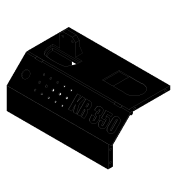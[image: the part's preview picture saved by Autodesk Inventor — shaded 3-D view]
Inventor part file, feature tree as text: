
AUTODESK INVENTOR PART (.ipt)
format: ipt  version: 2020 (Build 240168000, 168)  size: 1,130,496 bytes
history: native  units: mm
features: sketch x33, extrude x30, projected_geometry x20, chamfer x5, plane x3, emboss x1
ambient origin geometry x8: Origin, YZ Plane, XZ Plane, XY Plane, X Axis, Y Axis, Z Axis, Center Point
bodies: Solid1 (feature_tree)
feature tree (92):
  extrude  "Extrusion1"  Depth=120.0mm
  extrude  "Extrusion2"  Depth=40.0mm
  extrude  "Extrusion3"  TaperAngle=135.0deg  [1 undecoded]
  extrude  "Extrusion4"  Depth=125.0mm
  extrude  "Extrusion5"  Depth=1.0mm
  extrude  "Extrusion6"  Depth=20.0mm
  extrude  "Extrusion7"  Depth=10.0mm TaperAngle=0.0deg
  extrude  "Extrusion8"  Depth=3.0mm
  extrude  "Extrusion9"  Depth=0.25mm
  extrude  "Extrusion10"  Depth=0.25mm
  extrude  "Extrusion11"  Depth=0.3mm
  extrude  "Extrusion17"  Depth=20.0mm TaperAngle=0.0deg
  extrude  "Extrusion18"  Depth=14.196mm
  extrude  "Extrusion19"  Depth=0.35mm TaperAngle=0.0deg
  extrude  "Extrusion20"  Depth=19.547688mm
  extrude  "Extrusion21"  Depth=0.3mm
  extrude  "Extrusion22"  Depth=0.3mm
  extrude  "Extrusion23"  Depth=0.3mm
  extrude  "Extrusion24"  Depth=0.3mm
  sketch  "Sketch25"  dims[d73=0.3mm d74=5.0mm d75=0.25mm d76=19.547688mm d77=0.35mm d78=0.0mm]
  chamfer  "Chamfer1"  Distance=20.0mm
  chamfer  "Chamfer2"  Distance=0.35mm
  sketch  "Sketch26"  dims[d79=0.3mm d80=5.0mm d81=0.25mm d82=19.547688mm d83=20.0mm d84=0.0mm]
  extrude  "Extrusion25"  Depth=20.0mm TaperAngle=0.0deg
  emboss  "Emboss1"
  plane  "Work Plane1"
  extrude  "Extrusion26"  Depth=10.0mm TaperAngle=0.0deg
  plane  "Work Plane2"
  extrude  "Extrusion27"  Depth=10.0mm TaperAngle=0.0deg
  plane  "Work Plane3"
  extrude  "Extrusion28"  Depth=10.0mm
  extrude  "Extrusion29"  Depth=10.0mm
  chamfer  "Chamfer3"  Distance=10.0mm
  extrude  "Extrusion30"  Depth=15.0mm
  extrude  "Extrusion31"  Depth=15.0mm
  extrude  "Extrusion32"  Depth=6.0mm
  extrude  "Extrusion33"  Depth=15.0mm
  extrude  "Extrusion34"  Depth=4.2mm
  chamfer  "Chamfer4"  Distance=3.0mm
  chamfer  "Chamfer5"  Distance=6.0mm
  extrude  "Extrusion35"  Depth=10.0mm
  sketch  "Sketch1"  dims[d0=55.0mm d1=120.0mm]
  sketch  "Sketch2"  dims[d2=50.0mm d3=40.0mm]
  projected_geometry  "Projected Loop1"
  sketch  "Sketch3"  dims[d4=135.0deg d5=135.0deg]
  sketch  "Sketch4"  dims[d6=5.0mm d7=125.0mm]
  projected_geometry  "Projected Loop2"
  projected_geometry  "Projected Loop3"
  sketch  "Sketch5"  dims[d8=190.0mm d9=1.0mm]
  sketch  "Sketch6"  dims[d10=1.0mm d11=20.0mm]
  sketch  "Sketch7"  dims[d12=3.0mm d13=10.0mm d14=0.0mm]
  sketch  "Sketch8"  dims[d15=3.0mm d16=0.3mm]
  sketch  "Sketch9"  dims[d18=5.0mm d19=0.25mm]
  sketch  "Sketch10"  dims[d21=0.25mm d22=0.25mm]
  sketch  "Sketch11"  dims[d23=0.0mm d24=0.0mm d25=0.3mm d26=5.0mm d27=0.25mm]
  sketch  "Sketch17"  dims[d28=2.0mm d29=20.0mm d30=0.0mm]
  projected_geometry  "Projected Loop7"
  sketch  "Sketch18"  dims[d36=5.0mm d37=14.196mm]
  sketch  "Sketch19"  dims[d38=0.3mm d39=5.0mm d40=0.25mm d41=0.35mm d42=0.0mm]
  projected_geometry  "Projected Loop8"
  sketch  "Sketch20"  dims[d43=0.3mm d44=5.0mm d45=0.25mm d46=19.547688mm]
  sketch  "Sketch21"  dims[d47=20.0mm d48=0.0mm d49=0.3mm d50=5.0mm d51=0.25mm d52=19.547688mm]
  projected_geometry  "Projected Loop9"
  projected_geometry  "Projected Loop10"
  sketch  "Sketch22"  dims[d53=0.35mm d54=0.0mm d55=0.3mm d56=5.0mm d57=0.25mm d58=19.547688mm]
  projected_geometry  "Projected Loop11"
  projected_geometry  "Projected Loop12"
  projected_geometry  "Projected Loop13"
  projected_geometry  "Projected Loop14"
  sketch  "Sketch23"  dims[d59=228.6mm d60=0.0mm d61=0.3mm d62=5.0mm d63=0.25mm d64=19.547688mm]
  sketch  "Sketch24"  dims[d65=0.35mm d66=0.0mm d67=0.3mm d68=5.0mm d69=0.25mm d70=19.547688mm d71=20.0mm d72=0.0mm]
  projected_geometry  "Projected Loop15"
  projected_geometry  "Projected Loop16"
  projected_geometry  "Projected Loop17"
  projected_geometry  "Projected Loop18"
  projected_geometry  "Projected Loop19"
  projected_geometry  "Projected Loop20"
  sketch  "Sketch27"  dims[d96=3.0mm d107=10.0mm d108=0.0mm]
  sketch  "Sketch28"  dims[d109=12.0mm d110=10.0mm d111=0.0mm]
  sketch  "Sketch29"  dims[d112=10.0mm d113=0.0mm d114=12.0mm]
  sketch  "Sketch30"  dims[d115=5.5mm d116=3.25mm d117=10.0mm d118=0.0mm]
  projected_geometry  "Projected Loop21"
  sketch  "Sketch31"  dims[d119=6.0mm d120=15.0mm]
  projected_geometry  "Projected Loop22"
  sketch  "Sketch32"  dims[d121=6.0mm d122=15.0mm]
  sketch  "Sketch33"  dims[d123=6.0mm d124=6.0mm]
  sketch  "Sketch34"  dims[d125=15.0mm d126=15.0mm]
  projected_geometry  "Projected Loop23"
  sketch  "Sketch35"  dims[d127=4.0mm d128=0.0mm d129=4.2mm]
  sketch  "Sketch36"  dims[d130=4.2mm]
  sketch  "Sketch37"  dims[d131=4.2mm]
  sketch  "Sketch38"  dims[d132=4.2mm d133=3.0mm d134=0.0mm d135=6.0mm d136=6.0mm d137=15.0mm d138=15.0mm d139=4.0mm d140=0.0mm d141=4.2mm d142=4.2mm d143=3.0mm d144=0.0mm d145=2.0mm d146=4.0mm d147=45.0deg d148=2.0mm d149=4.0mm d150=45.0deg d151=22.2mm d152=6.4mm d153=6.4mm d154=6.4mm d155=6.4mm d156=6.4mm d157=30.0mm d158=40.0mm d159=43.2mm d160=21.4mm d161=21.4mm d162=21.4mm d163=21.4mm d164=10.0mm d165=13.2mm d166=0.0mm d167=0.0mm d168=5.1mm d169=5.1mm d170=5.1mm d171=5.1mm d172=5.1mm d173=3.0mm d174=0.0mm d175=22.2mm d176=6.4mm d177=6.4mm d178=6.4mm d179=6.4mm d180=6.4mm d181=30.0mm d182=40.0mm d183=43.2mm d184=21.4mm d185=21.4mm d186=21.4mm d187=21.4mm d188=10.0mm d189=13.2mm d190=0.0mm d191=0.0mm d192=5.1mm d193=5.1mm d194=5.1mm d195=5.1mm d196=5.1mm d197=1.0mm d198=0.0mm d199=5.2mm d200=50.0mm d201=6.0mm d202=10.0mm d203=3.0mm d204=10.0mm d205=0.0mm d206=160.0mm d207=10.0mm d208=0.0mm d209=266.0mm d210=10.0mm d211=0.0mm d212=6.0mm d213=6.0mm d214=6.0mm d215=10.0mm d216=0.0mm d217=10.0mm d218=4.0mm d219=45.0deg d299=27.0mm d300=67.21989mm d301=67.21989mm d302=52.0mm d303=74.5mm d304=26.0mm d305=26.0mm d306=121.0mm d307=0.25mm d308=0.25mm d309=0.25mm d310=0.25mm d311=3.5mm d312=0.0mm d313=32.75mm d314=2.5mm d315=0.0mm d316=72.0mm d317=91.999999mm d318=81.999999mm d319=167.166667mm d320=45.750001mm d321=45.750001mm d322=50.750001mm d323=172.166667mm d324=50.750001mm d325=7.0mm d326=7.0mm d327=2.0mm d328=2.0mm d329=5.0mm d330=32.384967mm d331=32.384967mm d332=22.0mm d333=0.15mm d334=5.0mm d335=0.0mm d336=72.0mm d337=91.999999mm d338=81.999999mm d339=167.166667mm d340=45.750001mm d341=45.750001mm d342=50.750001mm d343=172.166667mm d344=50.750001mm d345=7.0mm d346=7.0mm d347=2.0mm d348=2.0mm d349=5.0mm d350=32.384967mm d351=32.384967mm d352=22.0mm d353=0.15mm d354=5.0mm d355=0.0mm d356=50.0mm d357=21.15mm d358=50.0mm d359=0.0mm d360=10.0mm d361=25.0mm d362=45.0deg d363=10.0mm d364=25.0mm d365=45.0deg d366=50.0mm d367=12.5mm d368=5.5mm d369=5.5mm d370=15.0mm d371=15.0mm d372=0.0mm d373=0.0mm d17=0.872665mm]
note: 1 required parameter value undecoded (feature->parameter linkage not recoverable at this tier; creation-order binding heuristic only, values carry confidence <= 0.55)
